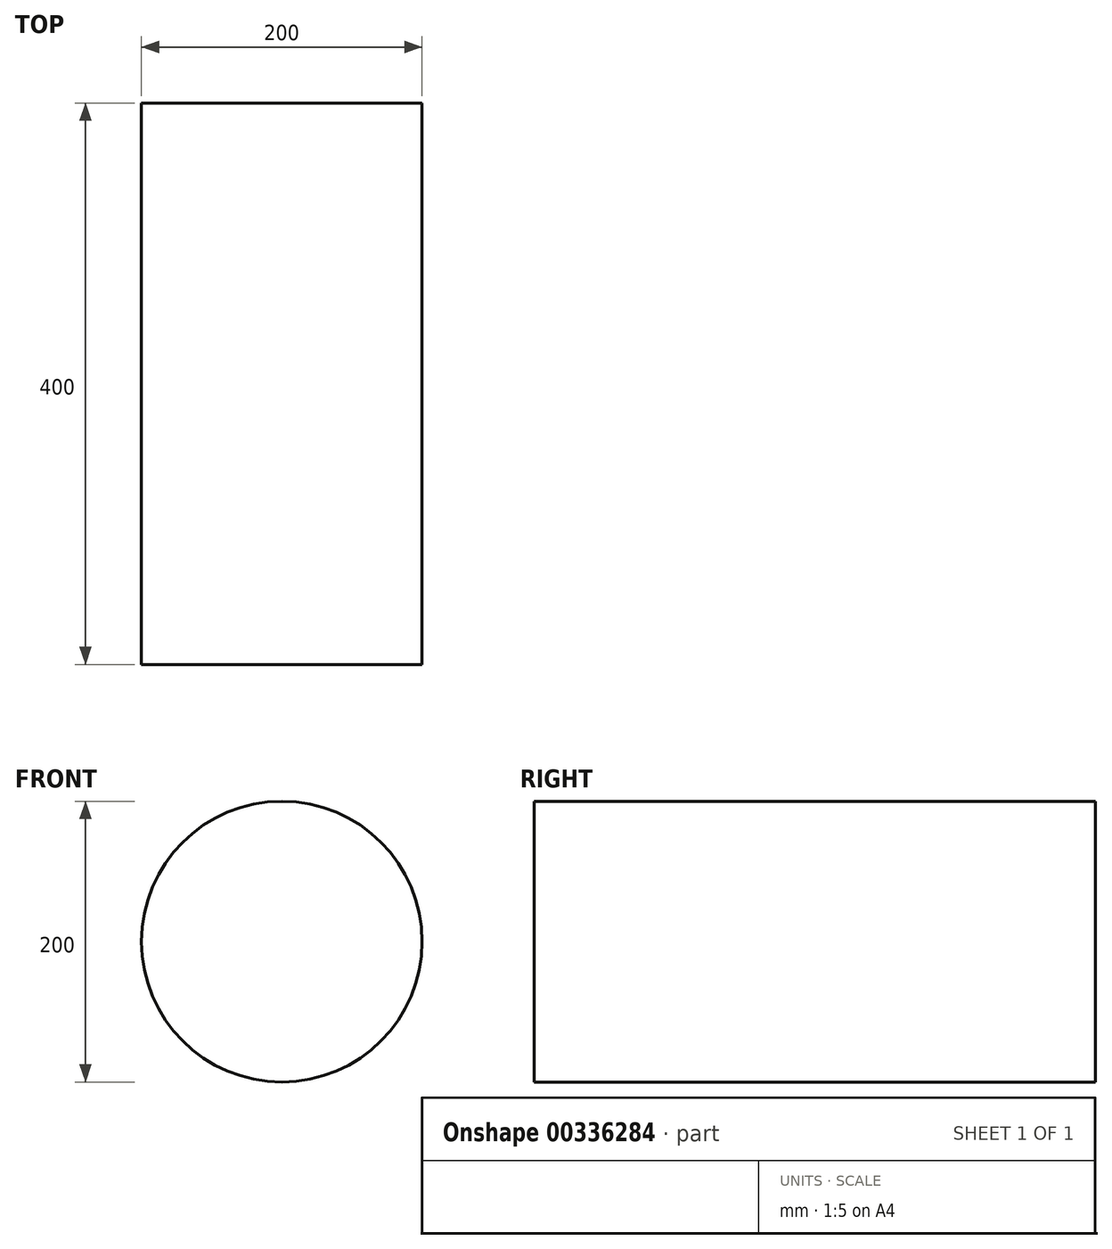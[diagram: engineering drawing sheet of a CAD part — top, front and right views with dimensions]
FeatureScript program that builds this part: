
annotation { "Feature Type Name" : "Feature", "Feature Type Description" : "" }
export const myFeature = defineFeature(function(context is Context, id is Id, definition is map)
    precondition{}
    {
        {
            var Q0;
            Q0=qCreatedBy(makeId("Front.planeOp"),FACE);
            var sketch = newSketch(context, id + "F0", { "sketchPlane" : qUnion([Q0])});
            skCircle(sketch, "E0", {"center": v(0, 0) * mm, "radius": 100 * mm});
            skSolve(sketch);
        }
        {
            var Q0;
            Q0=makeQuery(id+"F0.imprint","IMPRINT",FACE,{"disambiguationData":[TD([[makeQuery(id+"F0.imprint","IMPRINT",EDGE,{"derivedFrom":sQuery(id+"F0.wireOp",EDGE,"E0")}),1.0]])]});
            extrude(context, id + "F1", {"entities" : qUnion([Q0]), "depth" : 400 * mm});
        }
    });
